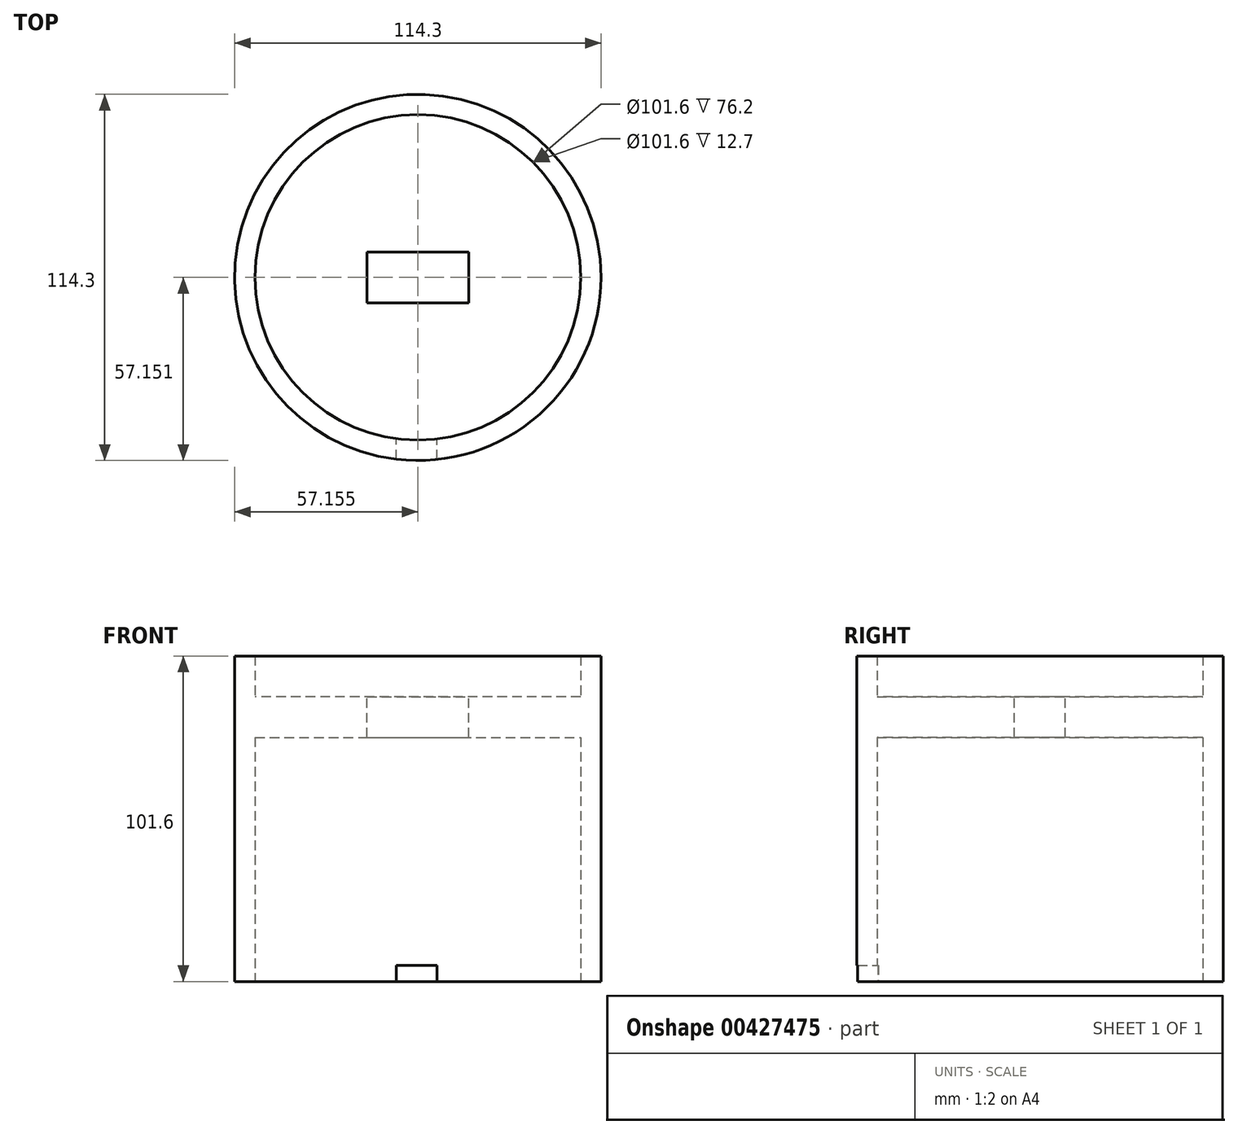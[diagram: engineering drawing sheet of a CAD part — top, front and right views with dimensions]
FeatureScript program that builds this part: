
annotation { "Feature Type Name" : "Feature", "Feature Type Description" : "" }
export const myFeature = defineFeature(function(context is Context, id is Id, definition is map)
    precondition{}
    {
        {
            var Q0;
            Q0=qCreatedBy(makeId("Top.planeOp"),FACE);
            var sketch = newSketch(context, id + "F0", { "sketchPlane" : qUnion([Q0])});
            skCircle(sketch, "E0", {"center": v(-87.3, 47.6) * mm, "radius": 57.15 * mm});
            skSolve(sketch);
        }
        {
            var Q0;
            Q0=makeQuery(id+"F0.imprint","IMPRINT",FACE,{"disambiguationData":[TD([[makeQuery(id+"F0.imprint","IMPRINT",EDGE,{"derivedFrom":sQuery(id+"F0.wireOp",EDGE,"E0")}),1.0]])]});
            extrude(context, id + "F1", {"entities" : qUnion([Q0]), "depth" : 88.9 * mm});
        }
        {
            var Q0;
            Q0=makeQuery(id+"F1.opExtrude","CAP_FACE",FACE,{"disambiguationData":[OSD([sQuery(id+"F0.wireOp",EDGE,"E0")])],"isStart":true});
            var sketch = newSketch(context, id + "F2", { "sketchPlane" : qUnion([Q0])});
            skCircle(sketch, "E1", {"center": v(-87.3, -47.6) * mm, "radius": 50.8 * mm});
            skSolve(sketch);
        }
        {
            var Q0;
            Q0 = qSketchRegion(id + "F2", true);
            extrude(context, id + "F3", {"entities" : qUnion([Q0]), "operationType" : NewBodyOperationType.REMOVE, "oppositeDirection" : true, "depth" : 76.2 * mm});
        }
        {
            var Q0;
            Q0=makeQuery(id+"F1.opExtrude","CAP_FACE",FACE,{"disambiguationData":[OSD([sQuery(id+"F0.wireOp",EDGE,"E0")])],"isStart":false});
            var sketch = newSketch(context, id + "F4", { "sketchPlane" : qUnion([Q0])});
            skLineSegment(sketch, "E2.bottom", {"start": v(-103.16, 55.57) * mm, "end": v(-71.4, 55.57) * mm});
            skLineSegment(sketch, "E2.top", {"start": v(-103.16, 39.7) * mm, "end": v(-71.4, 39.7) * mm});
            skLineSegment(sketch, "E2.left", {"start": v(-103.16, 55.57) * mm, "end": v(-103.16, 39.7) * mm});
            skLineSegment(sketch, "E2.right", {"start": v(-71.4, 55.57) * mm, "end": v(-71.4, 39.7) * mm});
            skSolve(sketch);
        }
        {
            var Q0;
            Q0=makeQuery(id+"F4.imprint","IMPRINT",FACE,{"disambiguationData":[TD([[makeQuery(id+"F4.imprint","IMPRINT",EDGE,{"derivedFrom":sQuery(id+"F4.wireOp",EDGE,"E2.bottom")}),-1.0]])]});
            extrude(context, id + "F5", {"entities" : qUnion([Q0]), "operationType" : NewBodyOperationType.REMOVE, "oppositeDirection" : true, "depth" : 12.7 * mm});
        }
        {
            var Q0;
            Q0=makeQuery(id+"F1.opExtrude","CAP_FACE",FACE,{"disambiguationData":[OSD([sQuery(id+"F0.wireOp",EDGE,"E0")])],"isStart":false});
            var sketch = newSketch(context, id + "F6", { "sketchPlane" : qUnion([Q0])});
            skCircle(sketch, "E3", {"center": v(-87.3, 47.6) * mm, "radius": 50.8 * mm});
            skSolve(sketch);
        }
        {
            var Q0;
            Q0=makeQuery(id+"F6.imprint","IMPRINT",FACE,{"disambiguationData":[TD([[makeQuery(id+"F6.imprint","IMPRINT",EDGE,{"derivedFrom":sQuery(id+"F6.wireOp",EDGE,"E3")}),-1.0]])]});
            extrude(context, id + "F7", {"entities" : qUnion([Q0]), "operationType" : NewBodyOperationType.ADD, "depth" : 12.7 * mm});
        }
        {
            var Q0;
            Q0=makeQuery(id+"F1.opExtrude","CAP_FACE",FACE,{"disambiguationData":[OSD([sQuery(id+"F0.wireOp",EDGE,"E0")])],"isStart":true});
            var sketch = newSketch(context, id + "F8", { "sketchPlane" : qUnion([Q0])});
            skLineSegment(sketch, "E4.bottom", {"start": v(-94.05, 14.02) * mm, "end": v(-81.35, 14.02) * mm});
            skLineSegment(sketch, "E4.top", {"start": v(-94.05, 0) * mm, "end": v(-81.35, 0) * mm});
            skLineSegment(sketch, "E4.left", {"start": v(-94.05, 14.02) * mm, "end": v(-94.05, 0) * mm});
            skLineSegment(sketch, "E4.right", {"start": v(-81.35, 14.02) * mm, "end": v(-81.35, 0) * mm});
            skSolve(sketch);
        }
        {
            var Q0;
            {var subQ0=sQuery(id+"F8.wireOp",EDGE,"E4.left");var subQ1=makeQuery(id+"F1.opExtrude","CAP_EDGE",EDGE,{"disambiguationData":[OSD([sQuery(id+"F0.wireOp",EDGE,"E0")])],"isStart":true});var subQ2=makeQuery(id+"F8.imprint","INTERSECT",VERTEX,{"derivedFrom":[subQ1,subQ0]});Q0=makeQuery(id+"F8.imprint","IMPRINT",FACE,{"disambiguationData":[TD([[makeQuery(id+"F8.imprint","IMPRINT",EDGE,{"disambiguationData":[TD([[subQ2,-1.0]])],"derivedFrom":subQ0}),1.0]])]});}
            var Q1;
            {var subQ0=sQuery(id+"F8.wireOp",EDGE,"E4.top");Q1=makeQuery(id+"F8.imprint","IMPRINT",FACE,{"disambiguationData":[TD([[makeQuery(id+"F8.imprint","IMPRINT",EDGE,{"derivedFrom":subQ0}),1.0]])]});}
            extrude(context, id + "F9", {"entities" : qUnion([Q0, Q1]), "operationType" : NewBodyOperationType.REMOVE, "oppositeDirection" : true, "depth" : 5.08 * mm});
        }
    });
